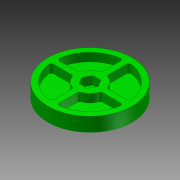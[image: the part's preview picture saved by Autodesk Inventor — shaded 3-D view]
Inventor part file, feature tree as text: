
AUTODESK INVENTOR PART (.ipt)
format: ipt  version: 2012 (Build 160160000, 160)  size: 163,328 bytes
history: native  units: mm
features: extrude x2, sketch x1, fillet x1
ambient origin geometry x8: Origin, YZ Plane, XZ Plane, XY Plane, X Axis, Y Axis, Z Axis, Center Point
bodies: Solid1 (feature_tree)
feature tree (4):
  sketch  "Sketch1"  dims[d0=60.0mm d1=10.0mm d2=52.0mm d3=20.0mm d4=2.0mm d5=40.0mm d7=360.0deg d9=6.0mm d10=4.0mm d11=0.0mm d12=10.0mm d13=0.0mm d14=2.0mm]
  extrude  "Extrusion1"  Depth=10.0mm
  extrude  "Extrusion2"  Depth=52.0mm
  fillet  "Fillet1"  Radius=20.0mm
